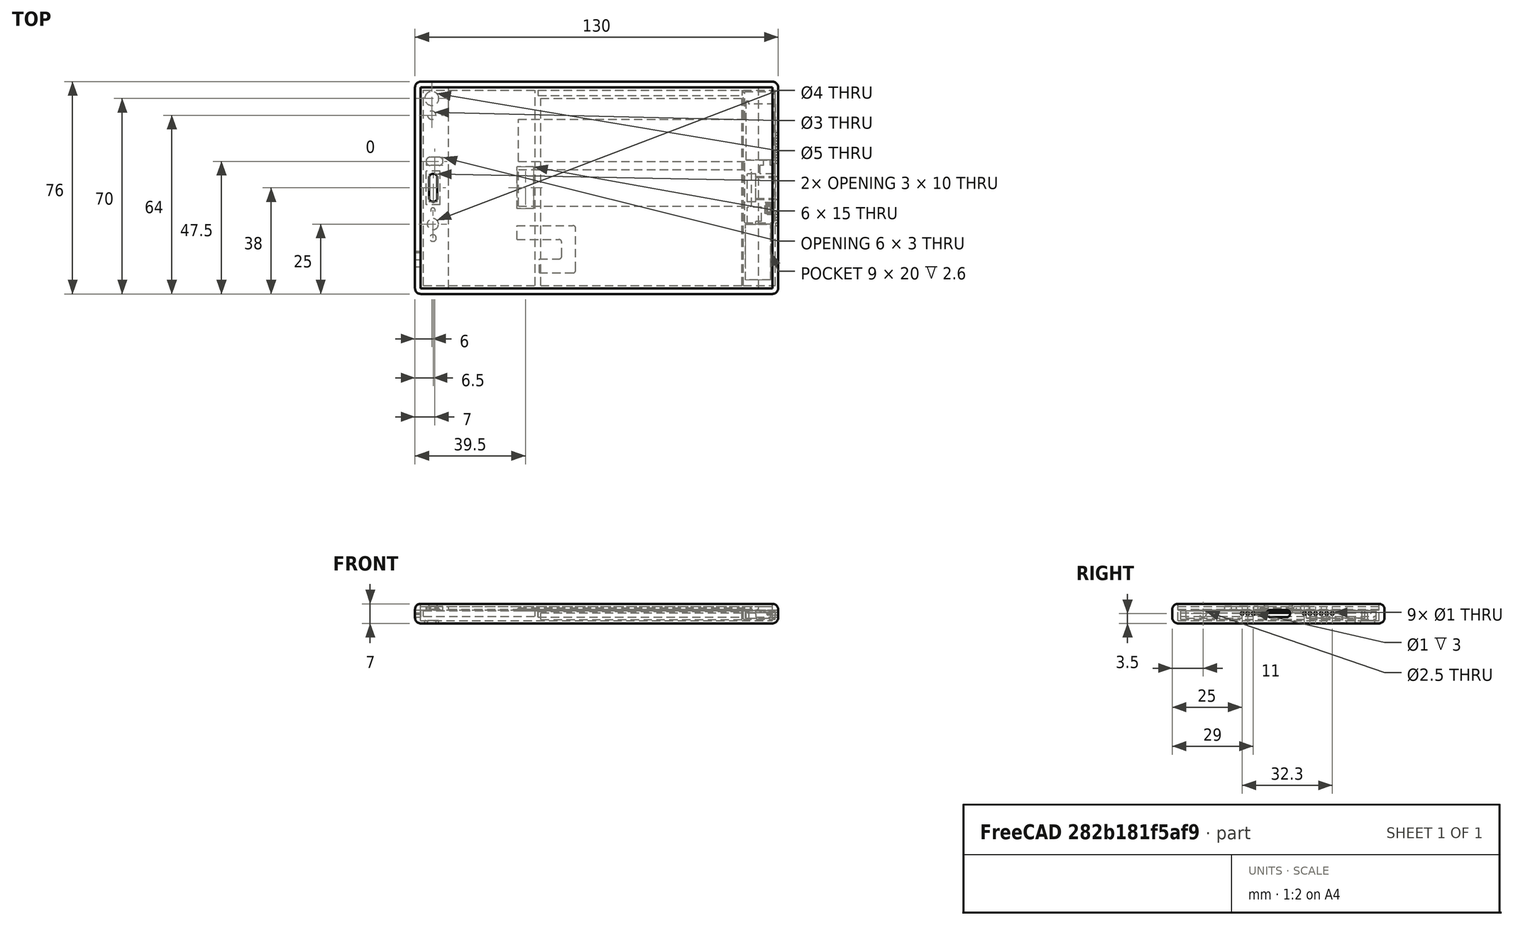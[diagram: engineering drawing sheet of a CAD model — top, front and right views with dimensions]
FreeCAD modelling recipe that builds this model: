
FCSTD DOCUMENT  (FreeCAD 0.16R6706 (Git))
Label: Febrero 2017
License: All rights reserved
LicenseURL: http://en.wikipedia.org/wiki/All_rights_reserved
objects: Part::Box×33, Part::Cut×28, Part::Cylinder×21, Part::MultiFuse×8, Part::Fillet×6, Part::Chamfer×1
note: 97 computed .brp shape members not serialized (recipe doc carries the construction recipe); baked Part::Feature solids carry a one-line shape summary decoded from their .brp

FEATURE [Part::Box] Box  label="Cubo"
  Height = 7
  Length = 130
  Width = 76
FEATURE [Part::Box] Box001  label="Cubo001"
  Height = 7
  Length = 126
  Placement = pos=(2,2,1) rot=(0,0,1;0rad)
  Width = 72
FEATURE [Part::Fillet] Fillet
  Base = -> Box
  Edges = 12 edges r=2: [Edge1,Edge2,Edge3,Edge4,Edge5,Edge6,Edge7,Edge8,Edge9,Edge10,Edge11,Edge12]
FEATURE [Part::Cut] Cut
  Base = -> Fillet
  Tool = -> Box001
FEATURE [Part::Box] Box002  label="touch not perfored"
  Height = 1
  Length = 126
  Placement = pos=(2,2,6) rot=(0,0,1;0rad)
  Width = 72
FEATURE [Part::Box] Box003  label="Cubo003"
  Height = 1
  Length = 10
  Placement = pos=(2,2,5) rot=(0,0,1;0rad)
  Width = 72
FEATURE [Part::Box] Box004  label="Cubo004"
  Height = 1
  Length = 5
  Placement = pos=(123,2,5) rot=(0,0,1;0rad)
  Width = 72
FEATURE [Part::Box] Box005  label="Cubo005"
  Height = 0.2
  Length = 126
  Placement = pos=(2,2,4.8) rot=(0,0,1;0rad)
  Width = 72
FEATURE [Part::Box] Box006  label="Screen 5,2""
  Height = 1
  Length = 111
  Placement = pos=(12,2,5) rot=(0,0,1;0rad)
  Width = 72
FEATURE [Part::Box] Box007  label="Cubo006"
  Height = 10
  Length = 3
  Placement = pos=(5,33,0) rot=(0,0,1;0rad)
  Width = 10
FEATURE [Part::Fillet] Fillet001  label="Ear speaker"
  Base = -> Box007
  Edges = 4 edges r=1.4: [Edge1,Edge3,Edge5,Edge7]
  Placement = pos=(0,0,2) rot=(0,0,1;0rad)
FEATURE [Part::Box] Box008  label="Cubo007"
  Height = 10
  Length = 5
  Placement = pos=(4,32,-4.5) rot=(0,0,1;0rad)
  Width = 12
FEATURE [Part::Cut] Cut001
  Base = -> Box003
  Tool = -> Fillet001
FEATURE [Part::Cut] Cut002
  Base = -> Box002
  Tool = -> Fillet001
FEATURE [Part::Cylinder] Cylinder  label="Cilindro"
  Angle = 360
  Height = 10
  Placement = pos=(6.4,30,0) rot=(0,0,1;0rad)
  Radius = 0.8
FEATURE [Part::Cylinder] Cylinder001  label="Cilindro001"
  Angle = 360
  Height = 10
  Placement = pos=(6.4,25,0) rot=(0,0,1;0rad)
  Radius = 2
FEATURE [Part::Cylinder] Cylinder002  label="Cilindro002"
  Angle = 360
  Height = 10
  Placement = pos=(6.4,20,0) rot=(0,0,1;0rad)
  Radius = 1.2
FEATURE [Part::MultiFuse] Fusion  label="LED, CAMERA, FLASH"
  Shapes = -> [Cylinder002,Cylinder001,Cylinder]
FEATURE [Part::Cut] Cut003
  Base = -> Cut001
  Tool = -> Fusion
FEATURE [Part::Cut] Cut004
  Base = -> Box005
  Tool = -> Fusion
FEATURE [Part::Box] Box009  label="Cubo008"
  Height = 10
  Length = 6
  Placement = pos=(4,46,0) rot=(0,0,1;0rad)
  Width = 3
FEATURE [Part::Fillet] Fillet002
  Base = -> Box009
  Edges = 4 edges r=1.4: [Edge1,Edge3,Edge5,Edge7]
FEATURE [Part::Cut] Cut005
  Base = -> Cut003
  Tool = -> Fillet002
FEATURE [Part::Cut] Cut006
  Base = -> Cut004
  Tool = -> Fillet002
FEATURE [Part::Cut] Cut007
  Base = -> Cut006
  Tool = -> Box008
FEATURE [Part::Box] Box010  label="Cubo009"
  Height = 10
  Length = 6
  Placement = pos=(36.5,30.5,0) rot=(0,0,1;0rad)
  Width = 15
FEATURE [Part::Cut] Cut008
  Base = -> Cut007
  Tool = -> Box010
FEATURE [Part::Box] Box011  label="PCB"
  Height = 2
  Length = 40
  Placement = pos=(3,3,2.5) rot=(0,0,1;0rad)
  Width = 70
FEATURE [Part::Box] Box012  label="Battery"
  Height = 2.5
  Length = 72
  Placement = pos=(45,3,1.3) rot=(0,0,1;0rad)
  Width = 67
FEATURE [Part::Box] Box013  label="Cubo012"
  Height = 3
  Length = 11.5
  Placement = pos=(117.5,3,1.5) rot=(0,0,1;0rad)
  Width = 70
FEATURE [Part::Box] Box014  label="Buzzer"
  Height = 3
  Length = 11.5
  Placement = pos=(117.5,3,1.5) rot=(0,0,1;0rad)
  Width = 70
FEATURE [Part::Cut] Cut009  label="Chassis no perfored"
  Base = -> Cut
  Tool = -> Box013
FEATURE [Part::Cylinder] Cylinder003  label="Antenna"
  Angle = 360
  Height = 73
  Placement = pos=(44,72,3.3) rot=(0.57735,0.57735,0.57735;2.0944rad)
  Radius = 1
FEATURE [Part::Cylinder] Cylinder004  label="Camera"
  Angle = 360
  Height = 10
  Placement = pos=(6,70,-5) rot=(0,0,1;0rad)
  Radius = 2.5
FEATURE [Part::Cylinder] Cylinder005  label="Camera lent"
  Angle = 360
  Height = 1
  Placement = pos=(6,70,0) rot=(0,0,1;0rad)
  Radius = 2.5
FEATURE [Part::Cut] Cut010
  Base = -> Cut009
  Tool = -> Cylinder004
FEATURE [Part::Cylinder] Cylinder006  label="FLASH"
  Angle = 360
  Height = 10
  Placement = pos=(6,64,-4) rot=(0,0,1;0rad)
  Radius = 1.5
FEATURE [Part::Cylinder] Cylinder007  label="FLASH lents"
  Angle = 360
  Height = 1
  Placement = pos=(6,64,0) rot=(0,0,1;0rad)
  Radius = 1.5
FEATURE [Part::Cut] Cut011
  Base = -> Cut010
  Tool = -> Cylinder006
FEATURE [Part::MultiFuse] Fusion001  label="Frame"
  Shapes = -> [Cut005,Cut008,Box004]
FEATURE [Part::Box] Box035  label="Cubo029"
  Height = 2.45
  Length = 8.65
  Width = 8.3
FEATURE [Part::Fillet] Fillet022  label="USB-C003"
  Base = -> Box035
  Edges = 4 edges r=1: [Edge9,Edge10,Edge11,Edge12]
  Placement = pos=(126,33.85,2.28) rot=(0,0,1;0rad)
FEATURE [Part::Cut] Cut012
  Base = -> Cut011
  Tool = -> Fillet022
FEATURE [Part::Box] Box036  label="Cubo030"
  Height = 2.45
  Length = 8.65
  Width = 8.3
FEATURE [Part::Fillet] Fillet023  label="USB-C004"
  Base = -> Box036
  Edges = 4 edges r=1: [Edge9,Edge10,Edge11,Edge12]
  Placement = pos=(122,33.85,2.28) rot=(0,0,1;0rad)
FEATURE [Part::Cut] Cut013
  Base = -> Box014
  Tool = -> Fillet023
FEATURE [Part::Cylinder] Cylinder008  label="Cilindro003"
  Angle = 360
  Height = 10
  Placement = pos=(-2,11,3.5) rot=(0.57735,0.57735,0.57735;2.0944rad)
  Radius = 1.25
FEATURE [Part::Cylinder] Cylinder009  label="Cilindro004"
  Angle = 360
  Height = 10
  Placement = pos=(-2,15,3.5) rot=(0.57735,0.57735,0.57735;2.0944rad)
  Radius = 0.25
FEATURE [Part::Cut] Cut014
  Base = -> Cut012
  Tool = -> Cylinder008
FEATURE [Part::Cylinder] Cylinder010  label="Cilindro005"
  Angle = 360
  Height = 10
  Placement = pos=(122,29,3.5) rot=(0.57735,0.57735,0.57735;2.0944rad)
  Radius = 0.5
FEATURE [Part::Cut] Cut015
  Base = -> Cut014
  Tool = -> Cylinder009
FEATURE [Part::Cylinder] Cylinder011  label="Cilindro006"
  Angle = 360
  Height = 10
  Placement = pos=(122,47.3,3.5) rot=(0.57735,0.57735,0.57735;2.0944rad)
  Radius = 0.5
FEATURE [Part::Cylinder] Cylinder012  label="Cilindro007"
  Angle = 360
  Height = 10
  Placement = pos=(122,27,3.5) rot=(0.57735,0.57735,0.57735;2.0944rad)
  Radius = 0.5
FEATURE [Part::Cylinder] Cylinder013  label="Cilindro008"
  Angle = 360
  Height = 10
  Placement = pos=(122,25,3.5) rot=(0.57735,0.57735,0.57735;2.0944rad)
  Radius = 0.5
FEATURE [Part::MultiFuse] Fusion002  label="Agujero micro"
  Shapes = -> [Cylinder010,Cylinder012,Cylinder013]
FEATURE [Part::Cylinder] Cylinder014  label="Cilindro009"
  Angle = 360
  Height = 10
  Placement = pos=(122,49.3,3.5) rot=(0.57735,0.57735,0.57735;2.0944rad)
  Radius = 0.5
FEATURE [Part::Cylinder] Cylinder015  label="Cilindro010"
  Angle = 360
  Height = 10
  Placement = pos=(122,51.3,3.5) rot=(0.57735,0.57735,0.57735;2.0944rad)
  Radius = 0.5
FEATURE [Part::Cylinder] Cylinder016  label="Cilindro011"
  Angle = 360
  Height = 10
  Placement = pos=(122,53.3,3.5) rot=(0.57735,0.57735,0.57735;2.0944rad)
  Radius = 0.5
FEATURE [Part::Cylinder] Cylinder017  label="Cilindro012"
  Angle = 360
  Height = 10
  Placement = pos=(122,55.3,3.5) rot=(0.57735,0.57735,0.57735;2.0944rad)
  Radius = 0.5
FEATURE [Part::Cylinder] Cylinder018  label="Cilindro013"
  Angle = 360
  Height = 10
  Placement = pos=(122,57.3,3.5) rot=(0.57735,0.57735,0.57735;2.0944rad)
  Radius = 0.5
FEATURE [Part::MultiFuse] Fusion003  label="Agujero altavoz"
  Shapes = -> [Cylinder014,Cylinder015,Cylinder016,Cylinder018,Cylinder017,Cylinder011]
FEATURE [Part::Cut] Cut016
  Base = -> Cut015
  Tool = -> Fusion002
FEATURE [Part::Cut] Cut017
  Base = -> Cut016
  Tool = -> Fusion003
FEATURE [Part::Box] Box037  label="Cubo031"
  Height = 4
  Length = 3
  Placement = pos=(119,33,3.8) rot=(0,0,1;0rad)
  Width = 10
FEATURE [Part::Cut] Cut018
  Base = -> Cut013
  Tool = -> Box037
FEATURE [Part::Box] Box038  label="Cubo032"
  Height = 10
  Length = 11
  Placement = pos=(118.5,48,1.9) rot=(0,0,1;0rad)
  Width = 20
FEATURE [Part::Cut] Cut019
  Base = -> Cut018
  Tool = -> Box038
FEATURE [Part::Box] Box039  label="Cubo033"
  Height = 10
  Length = 1
  Placement = pos=(118.5,67,1.9) rot=(0,0,1;0rad)
  Width = 2
FEATURE [Part::Cut] Cut020
  Base = -> Cut019
  Tool = -> Box039
FEATURE [Part::Box] Box040  label="Cubo034"
  Height = 10
  Length = 5
  Placement = pos=(123.5,43,3.9) rot=(0,0,1;0rad)
  Width = 3
FEATURE [Part::Box] Box041  label="Cubo035"
  Height = 10
  Length = 2.5
  Placement = pos=(124.75,43,3.9) rot=(0,0,1;0rad)
  Width = 6
FEATURE [Part::MultiFuse] Fusion004  label="Flex Loud Speaker"
  Shapes = -> [Box040,Box041]
FEATURE [Part::Cut] Cut021
  Base = -> Cut020
  Tool = -> Fusion004
FEATURE [Part::Box] Box042  label="Cubo036"
  Height = 10
  Length = 2.5
  Placement = pos=(125.5,29,3.9) rot=(0,0,1;0rad)
  Width = 3.5
FEATURE [Part::Chamfer] Chamfer
  Base = -> Box042
  Edges = 4 edges r=0.5: [Edge4,Edge8,Edge9,Edge11]
  Placement = pos=(0,0,-0.5) rot=(0,0,1;0rad)
FEATURE [Part::Cut] Cut022
  Base = -> Cut021
  Tool = -> Chamfer
FEATURE [Part::Cylinder] Cylinder019  label="Cilindro014"
  Angle = 360
  Height = 10
  Placement = pos=(126,29,3.5) rot=(0.57735,0.57735,0.57735;2.0944rad)
  Radius = 0.5
FEATURE [Part::Box] Box043  label="Cubo037"
  Height = 10
  Length = 3
  Placement = pos=(125.3,28.75,4) rot=(0,0,1;0rad)
  Width = 4
FEATURE [Part::Cut] Cut023
  Base = -> Cut022
  Tool = -> Box043
FEATURE [Part::Cut] Cut024
  Base = -> Cut023
  Tool = -> Cylinder019
FEATURE [Part::Cylinder] Cylinder020  label="Cilindro015"
  Angle = 360
  Height = 2
  Placement = pos=(126.75,29.3,3.5) rot=(0.57735,0.57735,0.57735;4.18879rad)
  Radius = 0.5
FEATURE [Part::Cut] Cut025
  Base = -> Cut024
  Tool = -> Cylinder020
FEATURE [Part::Box] Box044  label="Cubo038"
  Height = 10
  Length = 9
  Placement = pos=(118.3,5,1.9) rot=(0,0,1;0rad)
  Width = 20
FEATURE [Part::Box] Box045  label="Cubo039"
  Height = 10
  Length = 3
  Placement = pos=(119,7,3.9) rot=(0,0,1;0rad)
  Width = 20
FEATURE [Part::Cut] Cut026
  Base = -> Cut025
  Tool = -> Box044
FEATURE [Part::Box] Box046  label="Cubo040"
  Height = 10
  Length = 5
  Placement = pos=(119,26,3.9) rot=(0,0,1;0rad)
  Width = 5
FEATURE [Part::MultiFuse] Fusion005  label="Flex motor"
  Shapes = -> [Box045,Box046]
FEATURE [Part::Cut] Cut027
  Base = -> Cut026
  Tool = -> Fusion005
FEATURE [Part::Box] Box047  label="Cubo041"
  Height = 0.2
  Length = 10.5
  Placement = pos=(118,25.5,4.55) rot=(0,0,1;0rad)
  Width = 47
FEATURE [Part::Box] Box048  label="Cubo042"
  Height = 0.2
  Length = 83.5
  Placement = pos=(37,47.5,4.55) rot=(0,0,1;0rad)
  Width = 15
FEATURE [Part::MultiFuse] Fusion006  label="Main Flex"
  Shapes = -> [Box047,Box048]
FEATURE [Part::Box] Box049  label="Screen Flex"
  Height = 0.2
  Length = 83.5
  Placement = pos=(37,31.5,5.3) rot=(0,0,1;0rad)
  Width = 13
FEATURE [Part::Box] Box050  label="Cubo043"
  Height = 0.2
  Length = 21
  Placement = pos=(37,19.5,5.3) rot=(0,0,1;0rad)
  Width = 5
FEATURE [Part::Box] Box051  label="Cubo044"
  Height = 0.2
  Length = 13
  Placement = pos=(45,7.5,5.3) rot=(0,0,1;0rad)
  Width = 5
FEATURE [Part::Box] Box052  label="Cubo045"
  Height = 0.2
  Length = 5
  Placement = pos=(53,7.5,5.3) rot=(0,0,1;0rad)
  Width = 13
FEATURE [Part::MultiFuse] Fusion007
  Placement = pos=(-0.5,0,-0.75) rot=(0,0,1;0rad)
  Shapes = -> [Box050,Box052,Box051]
FEATURE [Part::Fillet] Fillet024
  Base = -> Fusion007
  Edges = 4 edges r=1: [Edge6,Edge9,Edge18,Edge21]
